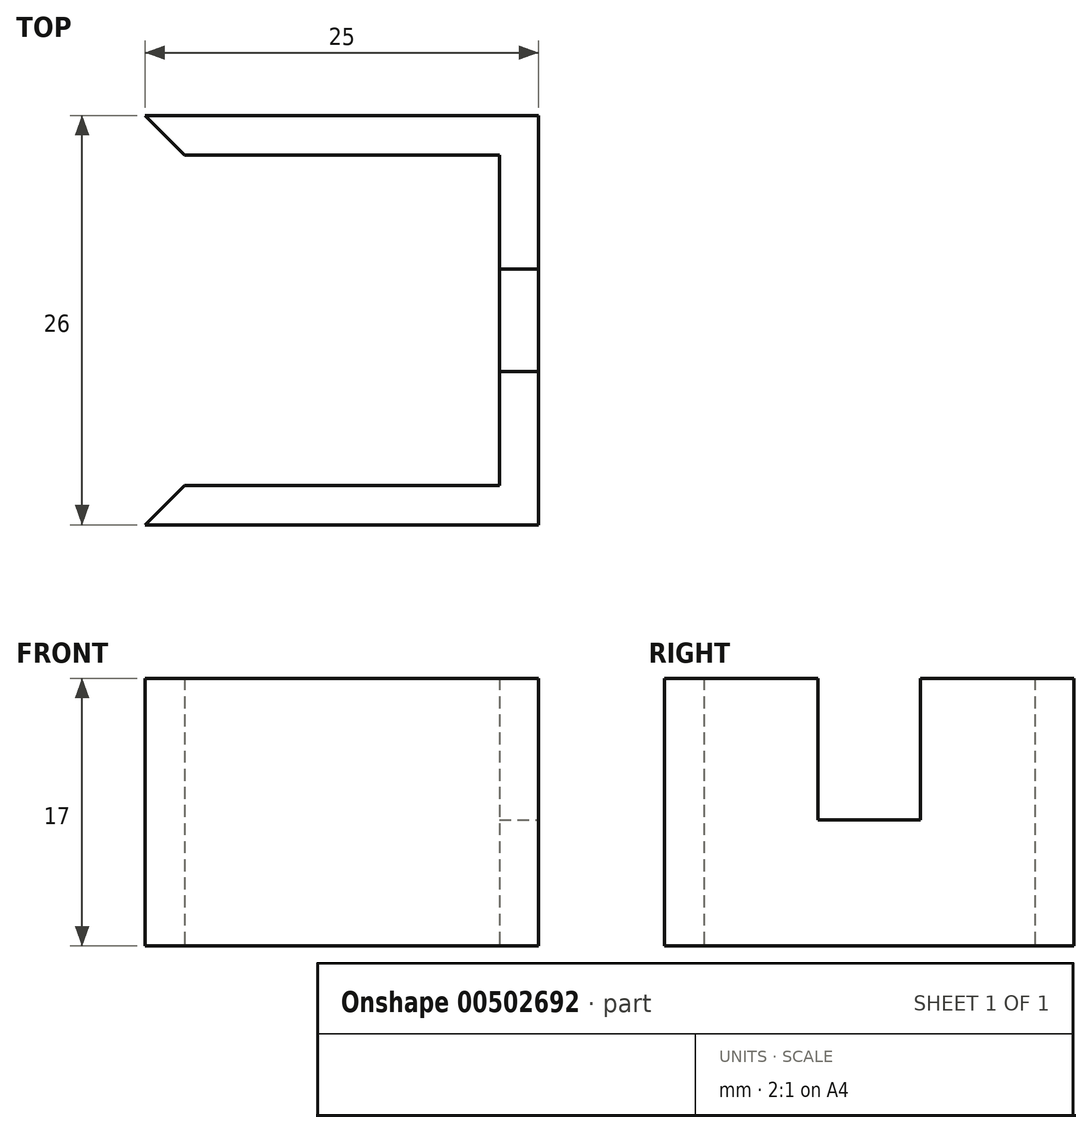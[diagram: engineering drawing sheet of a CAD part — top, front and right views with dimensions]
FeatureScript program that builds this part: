
annotation { "Feature Type Name" : "Feature", "Feature Type Description" : "" }
export const myFeature = defineFeature(function(context is Context, id is Id, definition is map)
    precondition{}
    {
        {
            var Q0;
            Q0=qCreatedBy(makeId("Top.planeOp"),FACE);
            var sketch = newSketch(context, id + "F0", { "sketchPlane" : qUnion([Q0])});
            skLineSegment(sketch, "E0.bottom", {"start": v(-12.6, -0.23) * mm, "end": v(7.4, -0.23) * mm});
            skLineSegment(sketch, "E0.top", {"start": v(-12.6, -21.23) * mm, "end": v(7.4, -21.23) * mm});
            skLineSegment(sketch, "E0.right", {"start": v(7.4, -0.23) * mm, "end": v(7.4, -21.23) * mm});
            skLineSegment(sketch, "E1.bottom", {"start": v(-15.1, 2.27) * mm, "end": v(9.9, 2.27) * mm});
            skLineSegment(sketch, "E1.top", {"start": v(-15.1, -23.73) * mm, "end": v(9.9, -23.73) * mm});
            skLineSegment(sketch, "E1.right", {"start": v(9.9, 2.27) * mm, "end": v(9.9, -23.73) * mm});
            skLineSegment(sketch, "E2", {"start": v(-15.1, 2.27) * mm, "end": v(-12.6, -0.23) * mm});
            skLineSegment(sketch, "E3", {"start": v(-12.6, -21.23) * mm, "end": v(-15.1, -23.73) * mm});
            skSolve(sketch);
        }
        {
            var Q0;
            Q0=makeQuery(id+"F0.imprint","IMPRINT",FACE,{"disambiguationData":[TD([[makeQuery(id+"F0.imprint","IMPRINT",EDGE,{"derivedFrom":sQuery(id+"F0.wireOp",EDGE,"E0.bottom")}),1.0]])]});
            extrude(context, id + "F1", {"entities" : qUnion([Q0]), "depth" : 17 * mm});
        }
        {
            var Q0;
            Q0=makeQuery(id+"F1.opExtrude","SWEPT_FACE",FACE,{"disambiguationData":[OSD([sQuery(id+"F0.wireOp",EDGE,"E1.right")])]});
            var sketch = newSketch(context, id + "F2", { "sketchPlane" : qUnion([Q0])});
            skLineSegment(sketch, "E4.bottom", {"start": v(-13.98, 17) * mm, "end": v(-7.48, 17) * mm});
            skLineSegment(sketch, "E4.top", {"start": v(-13.98, 8) * mm, "end": v(-7.48, 8) * mm});
            skLineSegment(sketch, "E4.left", {"start": v(-13.98, 17) * mm, "end": v(-13.98, 8) * mm});
            skLineSegment(sketch, "E4.right", {"start": v(-7.48, 17) * mm, "end": v(-7.48, 8) * mm});
            skSolve(sketch);
        }
        {
            var Q0;
            Q0=makeQuery(id+"F2.imprint","IMPRINT",FACE,{"disambiguationData":[TD([[makeQuery(id+"F2.imprint","IMPRINT",EDGE,{"derivedFrom":sQuery(id+"F2.wireOp",EDGE,"E4.bottom")}),1.0]])]});
            extrude(context, id + "F3", {"entities" : qUnion([Q0]), "operationType" : NewBodyOperationType.REMOVE, "oppositeDirection" : true, "depth" : 25 * mm});
        }
    });
